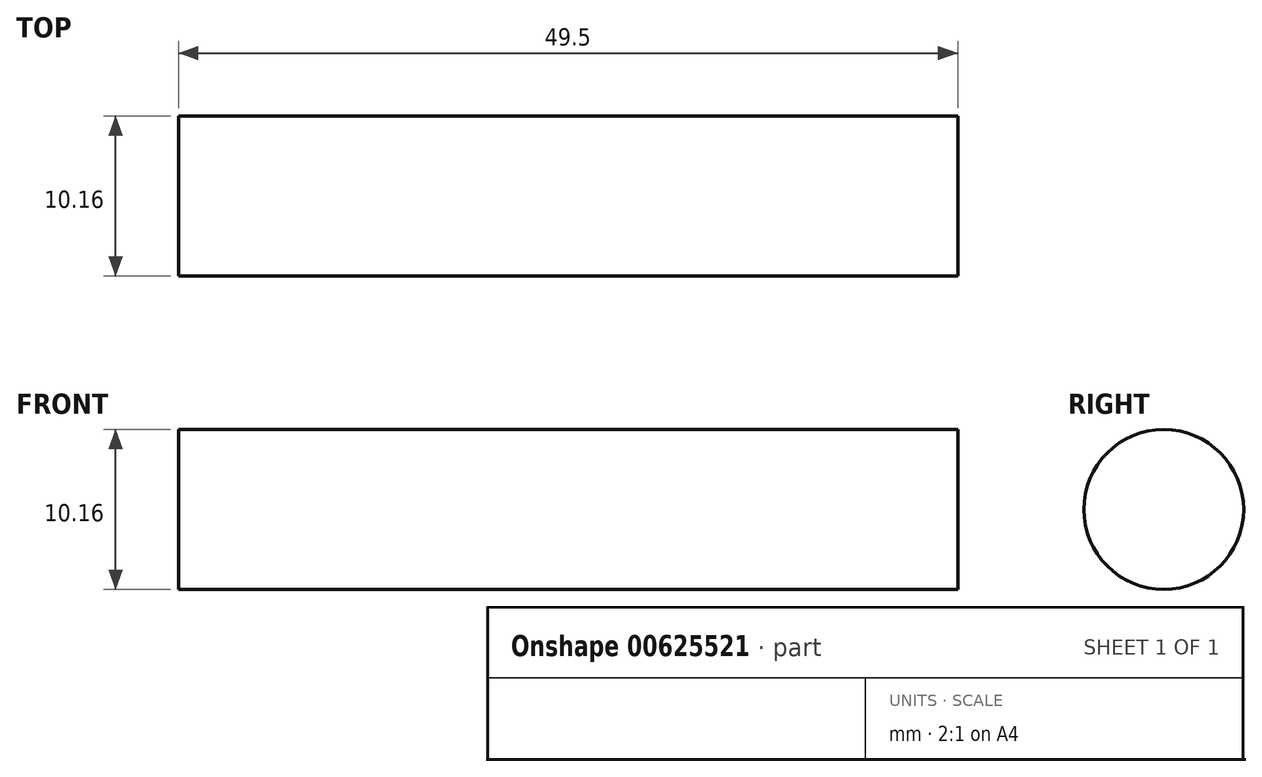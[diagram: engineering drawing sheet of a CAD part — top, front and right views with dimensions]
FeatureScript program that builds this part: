
annotation { "Feature Type Name" : "Feature", "Feature Type Description" : "" }
export const myFeature = defineFeature(function(context is Context, id is Id, definition is map)
    precondition{}
    {
        {
            var Q0;
            Q0=qCreatedBy(makeId("Right.planeOp"),FACE);
            var sketch = newSketch(context, id + "F0", { "sketchPlane" : qUnion([Q0])});
            skCircle(sketch, "E0", {"center": v(0, 0) * mm, "radius": 5.08 * mm});
            skSolve(sketch);
        }
        {
            var Q0;
            Q0 = qSketchRegion(id + "F0", true);
            extrude(context, id + "F1", {"entities" : qUnion([Q0]), "depth" : 49.5 * mm, "offsetDistance" : 25 * mm});
        }
    });
